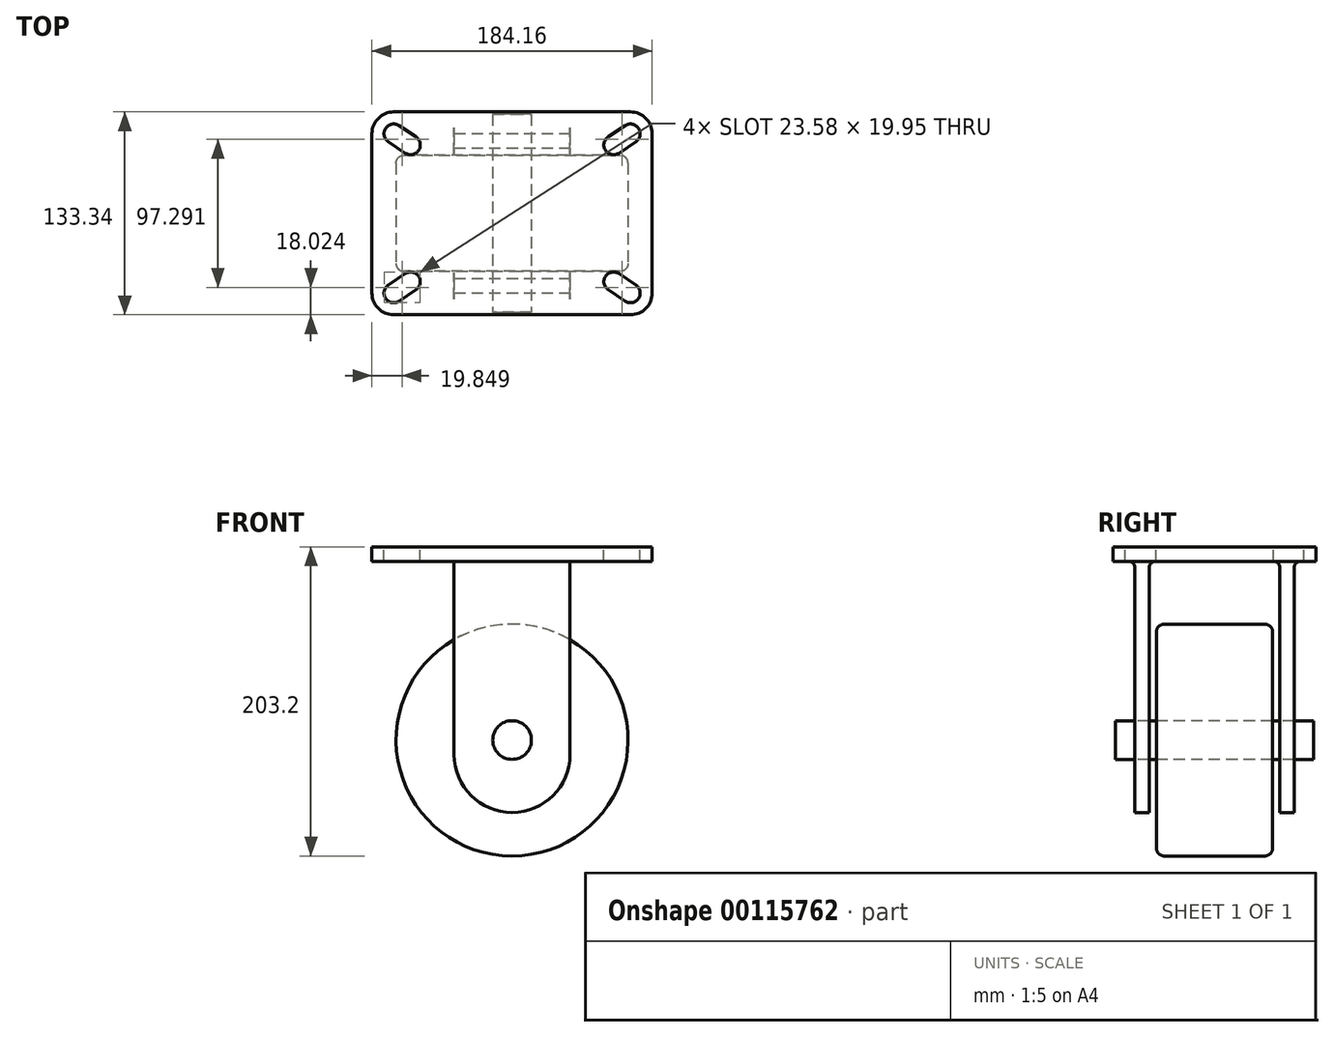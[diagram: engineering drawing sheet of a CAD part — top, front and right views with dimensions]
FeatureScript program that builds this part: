
annotation { "Feature Type Name" : "Feature", "Feature Type Description" : "" }
export const myFeature = defineFeature(function(context is Context, id is Id, definition is map)
    precondition{}
    {
        {
            var Q0;
            Q0=qCreatedBy(makeId("Top.planeOp"),FACE);
            var sketch = newSketch(context, id + "F0", { "sketchPlane" : qUnion([Q0])});
            skLineSegment(sketch, "E0.bottom", {"start": v(77.79, -66.68) * mm, "end": v(-77.79, -66.68) * mm});
            skLineSegment(sketch, "E0.top", {"start": v(77.79, 66.68) * mm, "end": v(-77.79, 66.68) * mm});
            skLineSegment(sketch, "E0.left", {"start": v(92.08, -52.39) * mm, "end": v(92.08, 52.39) * mm});
            skLineSegment(sketch, "E0.right", {"start": v(-92.08, -52.39) * mm, "end": v(-92.08, 52.39) * mm});
            skPoint(sketch, "E0.middle", {"position": v(0, 0) * mm});
            skArc(sketch, "E1", {"start": v(-77.79, 66.68) * mm, "mid": v(-87.9, 62.5) * mm, "end": v(-92.08, 52.39) * mm});
            skArc(sketch, "E2", {"start": v(92.07, 52.39) * mm, "mid": v(87.9, 62.5) * mm, "end": v(77.79, 66.68) * mm});
            skArc(sketch, "E3", {"start": v(-92.07, -52.39) * mm, "mid": v(-87.9, -62.5) * mm, "end": v(-77.79, -66.67) * mm});
            skArc(sketch, "E4", {"start": v(77.79, -66.67) * mm, "mid": v(87.9, -62.5) * mm, "end": v(92.08, -52.39) * mm});
            skPoint(sketch, "E5.orphan", {"position": v(92.08, 66.68) * mm});
            skPoint(sketch, "E6.orphan", {"position": v(92.08, -66.68) * mm});
            skPoint(sketch, "E7.orphan", {"position": v(-92.08, -66.68) * mm});
            skPoint(sketch, "E8.orphan", {"position": v(-92.08, 66.68) * mm});
            skArc(sketch, "E9", {"start": v(-74.24, 57.65) * mm, "mid": v(-83.05, 55.93) * mm, "end": v(-81.33, 47.12) * mm});
            skArc(sketch, "E10", {"start": v(81.33, 47.12) * mm, "mid": v(83.05, 55.93) * mm, "end": v(74.24, 57.65) * mm});
            skArc(sketch, "E11", {"start": v(74.24, -57.65) * mm, "mid": v(83.05, -55.93) * mm, "end": v(81.33, -47.12) * mm});
            skArc(sketch, "E12", {"start": v(-81.33, -47.12) * mm, "mid": v(-83.05, -55.93) * mm, "end": v(-74.24, -57.65) * mm});
            skArc(sketch, "E13", {"start": v(-70.22, 39.64) * mm, "mid": v(-61.4, 41.36) * mm, "end": v(-63.13, 50.17) * mm});
            skArc(sketch, "E14", {"start": v(63.13, 50.17) * mm, "mid": v(61.4, 41.36) * mm, "end": v(70.22, 39.64) * mm});
            skArc(sketch, "E15", {"start": v(-63.13, -50.17) * mm, "mid": v(-61.4, -41.36) * mm, "end": v(-70.22, -39.64) * mm});
            skArc(sketch, "E16", {"start": v(70.22, -39.64) * mm, "mid": v(61.4, -41.36) * mm, "end": v(63.13, -50.17) * mm});
            skLineSegment(sketch, "E17", {"start": v(-74.24, 57.65) * mm, "end": v(-63.13, 50.17) * mm});
            skLineSegment(sketch, "E18", {"start": v(-81.33, 47.12) * mm, "end": v(-70.22, 39.64) * mm});
            skLineSegment(sketch, "E19", {"start": v(63.13, 50.17) * mm, "end": v(74.24, 57.65) * mm});
            skLineSegment(sketch, "E20", {"start": v(70.22, 39.64) * mm, "end": v(81.33, 47.12) * mm});
            skLineSegment(sketch, "E21", {"start": v(70.22, -39.64) * mm, "end": v(81.33, -47.12) * mm});
            skLineSegment(sketch, "E22", {"start": v(63.13, -50.17) * mm, "end": v(74.24, -57.65) * mm});
            skLineSegment(sketch, "E23", {"start": v(-74.24, -57.65) * mm, "end": v(-63.13, -50.17) * mm});
            skLineSegment(sketch, "E24", {"start": v(-81.33, -47.12) * mm, "end": v(-70.22, -39.64) * mm});
            skSolve(sketch);
        }
        {
            var Q0;
            Q0=qSketchRegion(id+"F0",true);
            extrude(context, id + "F1", {"entities" : qUnion([Q0]), "oppositeDirection" : true, "depth" : 9.52 * mm});
        }
        {
            var Q0;
            Q0=qCreatedBy(makeId("Right.planeOp"),FACE);
            cPlane(context, id + "F2", {"entities" : qUnion([Q0]), "cplaneType" : CPlaneType.OFFSET, "offset" : 38.1 * mm, "width" : 152.4 * mm, "height" : 152.4 * mm});
        }
        {
            var Q0;
            Q0=qCreatedBy(id+"F2.planeOp",FACE);
            var sketch = newSketch(context, id + "F3", { "sketchPlane" : qUnion([Q0])});
            skLineSegment(sketch, "E25.0", {"start": v(-66.68, -9.53) * mm, "end": v(-66.68, 0) * mm});
            skLineSegment(sketch, "E25.1", {"start": v(-66.67, 0) * mm, "end": v(-52.39, 0) * mm});
            skLineSegment(sketch, "E25.2", {"start": v(-66.67, -9.53) * mm, "end": v(-52.39, -9.53) * mm});
            skLineSegment(sketch, "E25.3", {"start": v(-52.39, 0) * mm, "end": v(52.39, 0) * mm});
            skLineSegment(sketch, "E25.4", {"start": v(-52.39, -9.53) * mm, "end": v(52.39, -9.53) * mm});
            skLineSegment(sketch, "E25.5", {"start": v(52.39, 0) * mm, "end": v(66.68, 0) * mm});
            skLineSegment(sketch, "E25.6", {"start": v(52.39, -9.53) * mm, "end": v(66.68, -9.53) * mm});
            skLineSegment(sketch, "E25.7", {"start": v(66.68, -9.53) * mm, "end": v(66.68, 0) * mm});
            skLineSegment(sketch, "E26", {"start": v(-52.39, -13.5) * mm, "end": v(-52.39, -174.63) * mm});
            skLineSegment(sketch, "E27.0", {"start": v(-42.86, -13.5) * mm, "end": v(-42.86, -174.63) * mm});
            skArc(sketch, "E28", {"start": v(-52.39, -13.5) * mm, "mid": v(-53.55, -10.69) * mm, "end": v(-56.36, -9.53) * mm});
            skArc(sketch, "E29", {"start": v(-38.9, -9.53) * mm, "mid": v(-41.7, -10.69) * mm, "end": v(-42.86, -13.5) * mm});
            skLineSegment(sketch, "E30.MirrorCS", {"start": v(42.86, -13.5) * mm, "end": v(42.86, -174.63) * mm});
            skLineSegment(sketch, "E31.MirrorCS", {"start": v(52.39, -13.5) * mm, "end": v(52.39, -174.63) * mm});
            skArc(sketch, "E32.MirrorCS", {"start": v(38.9, -9.53) * mm, "mid": v(41.7, -10.69) * mm, "end": v(42.86, -13.5) * mm});
            skArc(sketch, "E33.MirrorCS", {"start": v(52.39, -13.5) * mm, "mid": v(53.55, -10.69) * mm, "end": v(56.36, -9.53) * mm});
            skLineSegment(sketch, "E34", {"start": v(-52.39, -174.63) * mm, "end": v(-42.86, -174.63) * mm});
            skLineSegment(sketch, "E35", {"start": v(42.86, -174.63) * mm, "end": v(52.39, -174.63) * mm});
            skSolve(sketch);
        }
        {
            var Q0;
            Q0 = qSketchRegion(id + "F3", true);
            extrude(context, id + "F4", {"entities" : qUnion([Q0]), "operationType" : NewBodyOperationType.ADD, "oppositeDirection" : true, "depth" : 76.2 * mm});
        }
        {
            var Q0;
            Q0=makeQuery(id+"F4.opExtrude","SWEPT_FACE",FACE,{"disambiguationData":[OSD([sQuery(id+"F3.wireOp",EDGE,"E26")])]});
            var sketch = newSketch(context, id + "F5", { "sketchPlane" : qUnion([Q0])});
            skArc(sketch, "E36", {"start": v(-38.1, -136.53) * mm, "mid": v(0, -174.63) * mm, "end": v(38.1, -136.53) * mm});
            skPoint(sketch, "E36.first.point", {"position": v(-38.1, -136.53) * mm});
            skPoint(sketch, "E36.second.point", {"position": v(0, -174.63) * mm});
            skPoint(sketch, "E36.third.point", {"position": v(38.1, -136.53) * mm});
            skLineSegment(sketch, "E37", {"start": v(-38.1, -136.53) * mm, "end": v(-38.1, -174.63) * mm});
            skLineSegment(sketch, "E38", {"start": v(-38.1, -174.63) * mm, "end": v(38.1, -174.63) * mm});
            skLineSegment(sketch, "E39", {"start": v(38.1, -174.63) * mm, "end": v(38.1, -136.53) * mm});
            skSolve(sketch);
        }
        {
            var Q0;
            Q0 = qSketchRegion(id + "F5", true);
            extrude(context, id + "F6", {"entities" : qUnion([Q0]), "operationType" : NewBodyOperationType.REMOVE, "endBound" : BoundingType.THROUGH_ALL, "oppositeDirection" : true, "depth" : 25.4 * mm});
        }
        {
            var Q0;
            Q0=qCreatedBy(makeId("Front.planeOp"),FACE);
            cPlane(context, id + "F7", {"entities" : qUnion([Q0]), "cplaneType" : CPlaneType.OFFSET, "offset" : 38.1 * mm, "width" : 152.4 * mm, "height" : 152.4 * mm});
        }
        {
            var Q0;
            Q0=qCreatedBy(id+"F7.planeOp",FACE);
            var sketch = newSketch(context, id + "F8", { "sketchPlane" : qUnion([Q0])});
            skLineSegment(sketch, "E40", {"start": v(0, 0) * mm, "end": v(0, -50.8) * mm});
            skCircle(sketch, "E41", {"center": v(0, -127) * mm, "radius": 76.2 * mm});
            skSolve(sketch);
        }
        {
            var Q0;
            Q0 = qSketchRegion(id + "F8", true);
            extrude(context, id + "F9", {"entities" : qUnion([Q0]), "oppositeDirection" : true, "depth" : 76.2 * mm});
        }
        {
            var Q0;
            Q0=makeQuery(id+"F9.opExtrude","CAP_EDGE",EDGE,{"disambiguationData":[OSD([sQuery(id+"F8.wireOp",EDGE,"E41")])],"isStart":true});
            var Q1;
            Q1=makeQuery(id+"F9.opExtrude","CAP_EDGE",EDGE,{"disambiguationData":[OSD([sQuery(id+"F8.wireOp",EDGE,"E41")])],"isStart":false});
            fillet(context, id + "F10", {"entities" : qUnion([Q0, Q1]), "radius" : 5.08 * mm, "tangentPropagation" : true, "allowEdgeOverflow" : false});
        }
        {
            var Q0;
            Q0=makeQuery(id+"F4.opExtrude","SWEPT_FACE",FACE,{"disambiguationData":[OSD([sQuery(id+"F3.wireOp",EDGE,"E26")])]});
            var sketch = newSketch(context, id + "F11", { "sketchPlane" : qUnion([Q0])});
            skCircle(sketch, "E42", {"center": v(0, -127) * mm, "radius": 12.7 * mm});
            skSolve(sketch);
        }
        {
            var Q0;
            Q0 = qSketchRegion(id + "F11", true);
            extrude(context, id + "F12", {"entities" : qUnion([Q0]), "oppositeDirection" : true, "depth" : 117.47 * mm, "hasSecondDirection" : true, "secondDirectionOppositeDirection" : false, "secondDirectionDepth" : 12.7 * mm});
        }
    });
